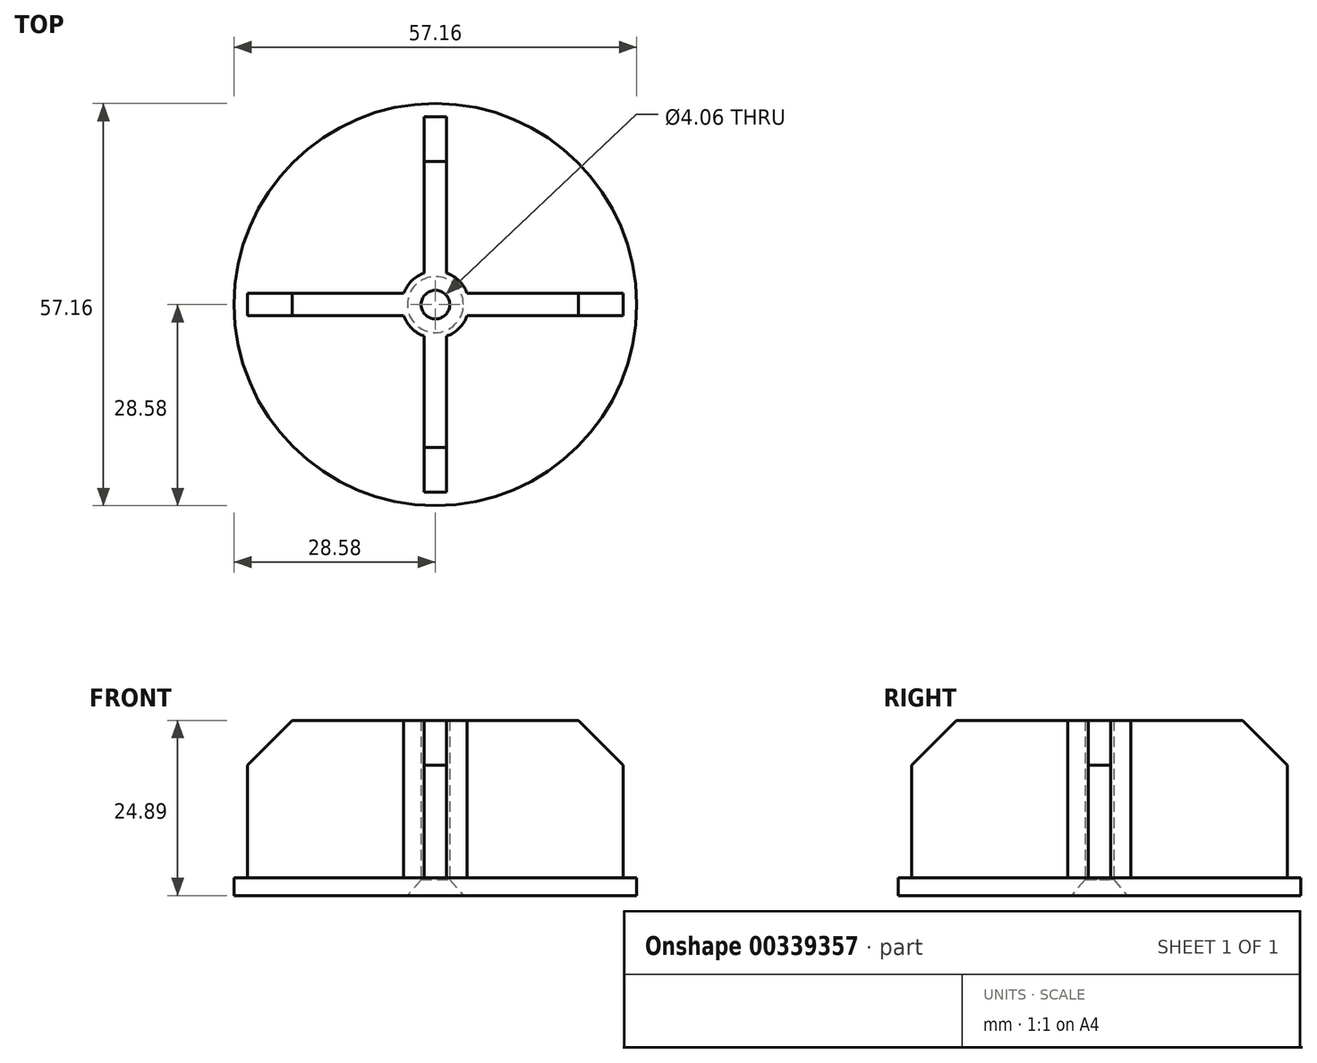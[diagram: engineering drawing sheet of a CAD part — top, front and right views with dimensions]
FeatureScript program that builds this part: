
annotation { "Feature Type Name" : "Feature", "Feature Type Description" : "" }
export const myFeature = defineFeature(function(context is Context, id is Id, definition is map)
    precondition{}
    {
        {
            var Q0;
            Q0=qCreatedBy(makeId("Top.planeOp"),FACE);
            var sketch = newSketch(context, id + "F0", { "sketchPlane" : qUnion([Q0])});
            skCircle(sketch, "E0", {"center": v(0, 0) * mm, "radius": 28.58 * mm});
            skSolve(sketch);
        }
        {
            var Q0;
            Q0 = qSketchRegion(id + "F0", true);
            extrude(context, id + "F1", {"entities" : qUnion([Q0]), "depth" : 2.54 * mm});
        }
        {
            var Q0;
            Q0=makeQuery(id+"F1.opExtrude","CAP_FACE",FACE,{"disambiguationData":[OSD([sQuery(id+"F0.wireOp",EDGE,"E0")])],"isStart":false});
            var sketch = newSketch(context, id + "F2", { "sketchPlane" : qUnion([Q0])});
            skLineSegment(sketch, "E1.bottom", {"start": v(26.67, 1.59) * mm, "end": v(1.59, 1.59) * mm});
            skLineSegment(sketch, "E1.top", {"start": v(26.67, -1.59) * mm, "end": v(1.59, -1.59) * mm});
            skLineSegment(sketch, "E1.left", {"start": v(26.67, 1.59) * mm, "end": v(26.67, -1.59) * mm});
            skLineSegment(sketch, "E1.right", {"start": v(-26.67, 1.59) * mm, "end": v(-26.67, -1.59) * mm});
            skPoint(sketch, "E1.middle", {"position": v(0, 0) * mm});
            skLineSegment(sketch, "E2.bottom", {"start": v(1.59, 26.67) * mm, "end": v(-1.59, 26.67) * mm});
            skLineSegment(sketch, "E2.top", {"start": v(1.59, -26.67) * mm, "end": v(-1.59, -26.67) * mm});
            skLineSegment(sketch, "E2.left", {"start": v(1.59, 26.67) * mm, "end": v(1.59, 1.59) * mm});
            skLineSegment(sketch, "E2.right", {"start": v(-1.59, 26.67) * mm, "end": v(-1.59, 1.59) * mm});
            skLineSegment(sketch, "E3.trimOffspring", {"start": v(-1.59, -1.59) * mm, "end": v(-26.67, -1.59) * mm});
            skLineSegment(sketch, "E4.trimOffspring", {"start": v(-1.59, -1.59) * mm, "end": v(-1.59, -26.67) * mm});
            skLineSegment(sketch, "E5.trimOffspring", {"start": v(-1.59, 1.59) * mm, "end": v(-26.67, 1.59) * mm});
            skLineSegment(sketch, "E6.trimOffspring", {"start": v(1.59, -1.59) * mm, "end": v(1.59, -26.67) * mm});
            skSolve(sketch);
        }
        {
            var Q0;
            Q0 = qSketchRegion(id + "F2", true);
            extrude(context, id + "F3", {"entities" : qUnion([Q0]), "operationType" : NewBodyOperationType.ADD, "depth" : 22.35 * mm});
        }
        {
            var Q0;
            Q0=makeQuery(id+"F3.opExtrude","CAP_EDGE",EDGE,{"disambiguationData":[OSD([sQuery(id+"F2.wireOp",EDGE,"E2.top")])],"isStart":false});
            var Q1;
            Q1=makeQuery(id+"F3.opExtrude","CAP_EDGE",EDGE,{"disambiguationData":[OSD([sQuery(id+"F2.wireOp",EDGE,"E1.left")])],"isStart":false});
            var Q2;
            Q2=makeQuery(id+"F3.opExtrude","CAP_EDGE",EDGE,{"disambiguationData":[OSD([sQuery(id+"F2.wireOp",EDGE,"E2.bottom")])],"isStart":false});
            var Q3;
            Q3=makeQuery(id+"F3.opExtrude","CAP_EDGE",EDGE,{"disambiguationData":[OSD([sQuery(id+"F2.wireOp",EDGE,"E1.right")])],"isStart":false});
            chamfer(context, id + "F4", {"entities" : qUnion([Q0, Q1, Q2, Q3]), "width" : 6.35 * mm, "tangentPropagation" : true});
        }
        {
            var Q0;
            Q0=makeQuery(id+"F3.opExtrude","CAP_FACE",FACE,{"disambiguationData":[OSD([sQuery(id+"F2.wireOp",EDGE,"E1.bottom"),sQuery(id+"F2.wireOp",EDGE,"E1.top"),sQuery(id+"F2.wireOp",EDGE,"E1.left"),sQuery(id+"F2.wireOp",EDGE,"E1.right"),sQuery(id+"F2.wireOp",EDGE,"E2.bottom"),sQuery(id+"F2.wireOp",EDGE,"E2.top"),sQuery(id+"F2.wireOp",EDGE,"E2.left"),sQuery(id+"F2.wireOp",EDGE,"E2.right"),sQuery(id+"F2.wireOp",EDGE,"E3.trimOffspring"),sQuery(id+"F2.wireOp",EDGE,"E4.trimOffspring"),sQuery(id+"F2.wireOp",EDGE,"E5.trimOffspring"),sQuery(id+"F2.wireOp",EDGE,"E6.trimOffspring")])],"isStart":false});
            var sketch = newSketch(context, id + "F5", { "sketchPlane" : qUnion([Q0])});
            skCircle(sketch, "E7", {"center": v(0, 0) * mm, "radius": 4.76 * mm});
            skSolve(sketch);
        }
        {
            var Q0;
            Q0 = qSketchRegion(id + "F5", true);
            var Q1;
            Q1=makeQuery(id+"F1.opExtrude","CAP_FACE",FACE,{"disambiguationData":[OSD([sQuery(id+"F0.wireOp",EDGE,"E0")])],"isStart":false});
            extrude(context, id + "F6", {"entities" : qUnion([Q0]), "operationType" : NewBodyOperationType.ADD, "endBound" : BoundingType.UP_TO_SURFACE, "oppositeDirection" : true, "endBoundEntityFace" : qUnion([Q1]), "depth" : 25.4 * mm});
        }
        {
            var Q0;
            Q0=makeQuery(id+"F1.opExtrude","CAP_FACE",FACE,{"disambiguationData":[OSD([sQuery(id+"F0.wireOp",EDGE,"E0")])],"isStart":true});
            var sketch = newSketch(context, id + "F7", { "sketchPlane" : qUnion([Q0])});
            skPoint(sketch, "E8", {"position": v(0, 0) * mm});
            skSolve(sketch);
        }
        {
            var Q0;
            Q0=sQuery(id+"F7.wireOp",VERTEX,"E8");
            var Q1;
            Q1=makeQuery(id+"F1.opExtrude","SWEPT_BODY",BODY,{"disambiguationData":[OSD([sQuery(id+"F0.wireOp",EDGE,"E0")])]});
            hole(context, id + "F8", {"style" : HoleStyle.C_SINK, "endStyle" : HoleEndStyle.THROUGH, "holeDiameter" : 4.06 * mm, "cSinkDiameter" : 7.95 * mm, "cSinkAngle" : 82 * degree, "tappedDepth" : 12.7 * mm, "tapClearance" : 3, "locations" : qUnion([Q0]), "scope" : qUnion([Q1])});
        }
    });
